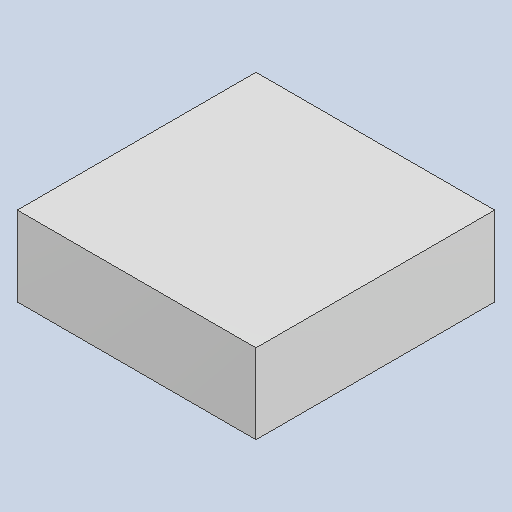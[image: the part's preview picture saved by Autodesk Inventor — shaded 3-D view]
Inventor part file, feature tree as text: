
AUTODESK INVENTOR PART (.ipt)
format: ipt  version: 2023.4 (Build 274418000, 418)  size: 79,872 bytes
history: native  units: mm
features: extrude x1
ambient origin geometry x8: Origin, YZ Plane, XZ Plane, XY Plane, X Axis, Y Axis, Z Axis, Center Point
bodies: Solid1 (feature_tree)
feature tree (1):
  extrude  "Extruded_37"  [1 undecoded]
note: 1 required parameter value undecoded (feature->parameter linkage not recoverable at this tier; creation-order binding heuristic only, values carry confidence <= 0.55)
